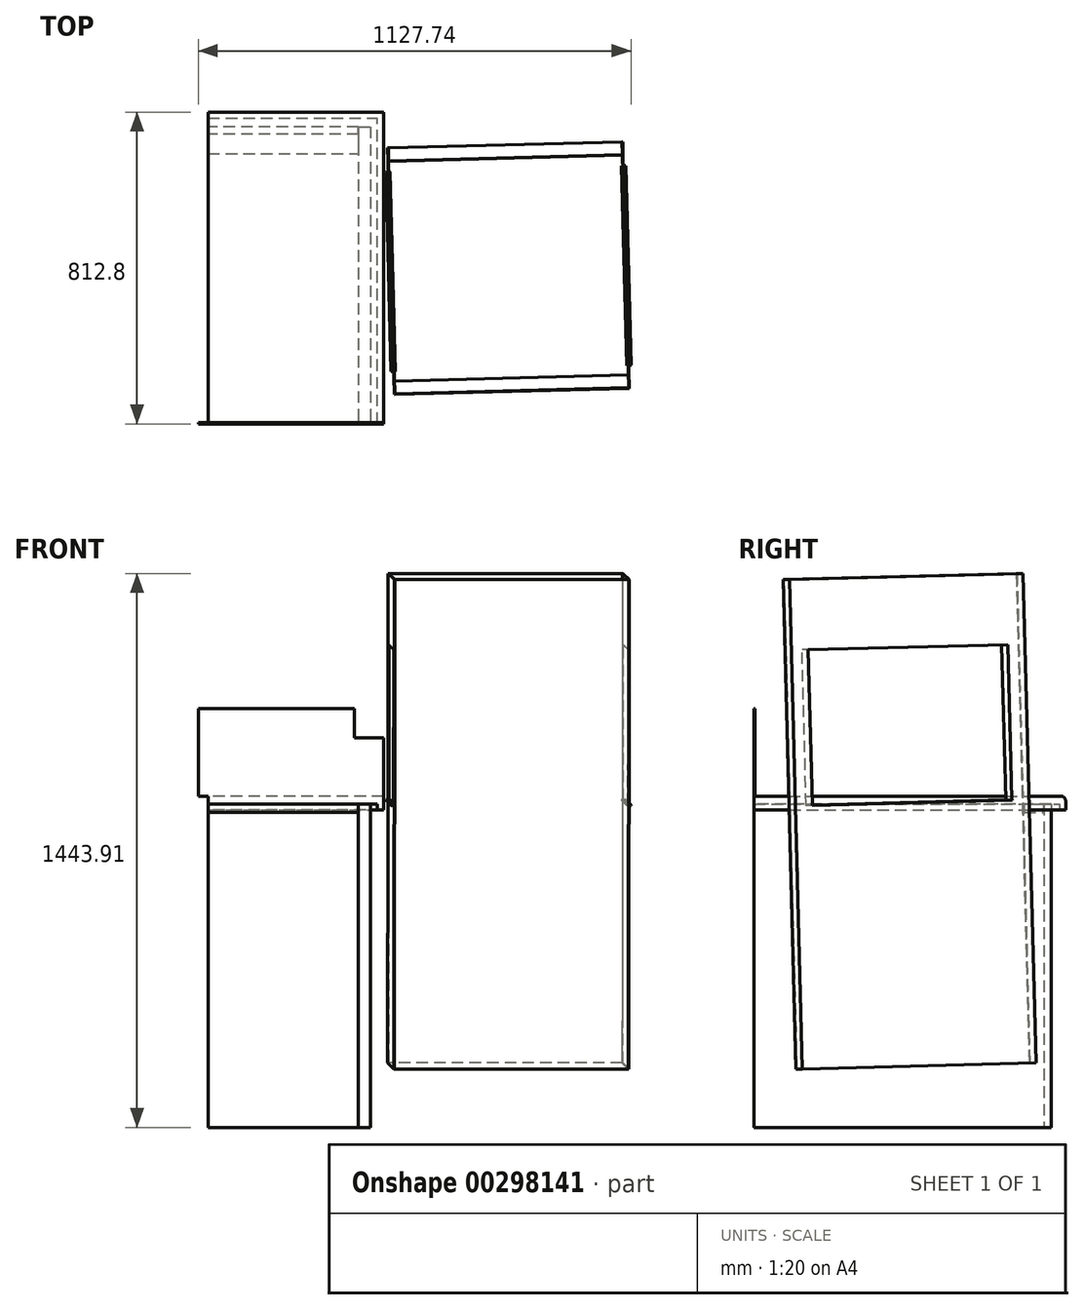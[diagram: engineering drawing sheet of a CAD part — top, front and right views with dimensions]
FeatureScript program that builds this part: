
annotation { "Feature Type Name" : "Feature", "Feature Type Description" : "" }
export const myFeature = defineFeature(function(context is Context, id is Id, definition is map)
    precondition{}
    {
        {
            var Q0;
            Q0=qCreatedBy(makeId("Top.planeOp"),FACE);
            cPlane(context, id + "F0", {"entities" : qUnion([Q0]), "cplaneType" : CPlaneType.OFFSET, "offset" : 863.6 * mm, "oppositeDirection" : true, "width" : 152.4 * mm, "height" : 152.4 * mm});
        }
        {
            var Q0;
            Q0=qCreatedBy(makeId("Right.planeOp"),FACE);
            var sketch = newSketch(context, id + "F1", { "sketchPlane" : qUnion([Q0])});
            skLineSegment(sketch, "E0.bottom", {"start": v(-406.4, 0) * mm, "end": v(393.7, 0) * mm});
            skLineSegment(sketch, "E0.top", {"start": v(-406.4, -36.51) * mm, "end": v(406.4, -36.51) * mm});
            skLineSegment(sketch, "E0.left", {"start": v(-406.4, 0) * mm, "end": v(-406.4, -36.51) * mm});
            skLineSegment(sketch, "E0.right", {"start": v(406.4, -12.7) * mm, "end": v(406.4, -36.51) * mm});
            skPoint(sketch, "E1.visualSharp", {"position": v(406.4, 0) * mm});
            skArc(sketch, "E1.filletArc", {"start": v(406.4, -12.7) * mm, "mid": v(402.68, -3.72) * mm, "end": v(393.7, 0) * mm});
            skSolve(sketch);
        }
        {
            var Q0;
            Q0 = qSketchRegion(id + "F1", true);
            extrude(context, id + "F2", {"entities" : qUnion([Q0]), "depth" : 457.2 * mm});
        }
        {
            var Q0;
            Q0=makeQuery(id+"F2.opExtrude","SWEPT_FACE",FACE,{"disambiguationData":[OSD([sQuery(id+"F1.wireOp",EDGE,"E0.top")])]});
            var sketch = newSketch(context, id + "F3", { "sketchPlane" : qUnion([Q0])});
            skLineSegment(sketch, "E2.bottom", {"start": v(0, 406.4) * mm, "end": v(441.33, 406.4) * mm});
            skLineSegment(sketch, "E2.top", {"start": v(0, -390.53) * mm, "end": v(441.33, -390.52) * mm});
            skLineSegment(sketch, "E2.left", {"start": v(0, 406.4) * mm, "end": v(0, -390.53) * mm});
            skLineSegment(sketch, "E2.right", {"start": v(441.33, 406.4) * mm, "end": v(441.33, -390.52) * mm});
            skSolve(sketch);
        }
        {
            var Q0;
            Q0 = qSketchRegion(id + "F3", true);
            extrude(context, id + "F4", {"entities" : qUnion([Q0]), "operationType" : NewBodyOperationType.REMOVE, "oppositeDirection" : true, "depth" : 15.88 * mm});
        }
        {
            var Q0;
            Q0=qCreatedBy(id+"F0.planeOp",FACE);
            var sketch = newSketch(context, id + "F5", { "sketchPlane" : qUnion([Q0])});
            skLineSegment(sketch, "E3", {"start": v(779.66, 121.89) * mm, "end": v(784.98, -81.25) * mm});
            skPoint(sketch, "E4", {"position": v(782.32, 20.32) * mm});
            skLineSegment(sketch, "E5", {"start": v(782.32, 223.52) * mm, "end": v(782.32, 20.32) * mm, "construction": true});
            skSolve(sketch);
        }
        {
            var Q0;
            Q0 = qSketchRegion(id + "F5", true);
            var Q1;
            Q1 = qConstructionFilter(qBodyType(qCreatedBy(id + "F5" ,EDGE), BodyType.WIRE), ConstructionObject.NO);
            extrude(context, id + "F6", {"entities" : qUnion([Q0]), "bodyType" : ToolBodyType.SURFACE, "surfaceEntities" : qUnion([Q1]), "depth" : 1524 * mm});
        }
        {
            var Q0;
            Q0=makeQuery(id+"F6.opExtrude","SWEPT_FACE",FACE,{"disambiguationData":[OSD([sQuery(id+"F5.wireOp",EDGE,"E3")])]});
            var sketch = newSketch(context, id + "F7", { "sketchPlane" : qUnion([Q0])});
            skLineSegment(sketch, "E6", {"start": v(0.17, -863.6) * mm, "end": v(40.07, 660.4) * mm});
            skSolve(sketch);
        }
        {
            var Q0;
            Q0 = qSketchRegion(id + "F7", true);
            var Q1;
            Q1=sQuery(id+"F7.wireOp",EDGE,"E6");
            extrude(context, id + "F8", {"entities" : qUnion([Q0]), "bodyType" : ToolBodyType.SURFACE, "surfaceEntities" : qUnion([Q1]), "endBound" : BoundingType.SYMMETRIC, "depth" : 203.2 * mm});
        }
        {
            var Q0;
            Q0=makeQuery(id+"F2.opExtrude","SWEPT_FACE",FACE,{"disambiguationData":[OSD([sQuery(id+"F1.wireOp",EDGE,"E0.left")])]});
            cPlane(context, id + "F9", {"entities" : qUnion([Q0]), "cplaneType" : CPlaneType.OFFSET, "offset" : 0 * mm, "width" : 152.4 * mm, "height" : 152.4 * mm});
        }
        {
            var Q0;
            Q0=qCreatedBy(id+"F9.planeOp",FACE);
            var sketch = newSketch(context, id + "F10", { "sketchPlane" : qUnion([Q0])});
            skLineSegment(sketch, "E7.bottom", {"start": v(457.2, 0) * mm, "end": v(274.53, 0) * mm});
            skLineSegment(sketch, "E7.top", {"start": v(457.2, 152.4) * mm, "end": v(381, 152.4) * mm});
            skLineSegment(sketch, "E7.left", {"start": v(457.2, 0) * mm, "end": v(457.2, 152.4) * mm});
            skLineSegment(sketch, "E8", {"start": v(381, 152.4) * mm, "end": v(381, 228.6) * mm});
            skLineSegment(sketch, "E9", {"start": v(381, 228.6) * mm, "end": v(-25.4, 228.6) * mm});
            skLineSegment(sketch, "E10", {"start": v(-25.4, 228.6) * mm, "end": v(-25.4, 0) * mm});
            skLineSegment(sketch, "E11", {"start": v(-25.4, 0) * mm, "end": v(274.53, 0) * mm});
            skSolve(sketch);
        }
        {
            var Q0;
            Q0=makeQuery(id+"F10.imprint","IMPRINT",FACE,{"disambiguationData":[TD([[makeQuery(id+"F10.imprint","IMPRINT",EDGE,{"derivedFrom":sQuery(id+"F10.wireOp",EDGE,"E7.bottom")}),-1.0]])]});
            extrude(context, id + "F11", {"entities" : qUnion([Q0]), "operationType" : NewBodyOperationType.ADD, "oppositeDirection" : true, "depth" : 3.17 * mm});
        }
        {
            var Q0;
            Q0=makeQuery(id+"F11.boolean.opBoolean","MERGE",FACE,{"derivedFrom":[makeQuery(id+"F2.opExtrude","CAP_FACE",FACE,{"disambiguationData":[OSD([sQuery(id+"F1.wireOp",EDGE,"E0.bottom"),sQuery(id+"F1.wireOp",EDGE,"E0.top"),sQuery(id+"F1.wireOp",EDGE,"E0.left"),sQuery(id+"F1.wireOp",EDGE,"E0.right"),sQuery(id+"F1.wireOp",EDGE,"E1.filletArc")])],"isStart":false}),makeQuery(id+"F11.opExtrude","SWEPT_FACE",FACE,{"disambiguationData":[OSD([sQuery(id+"F10.wireOp",EDGE,"E7.left")])]})]});
            cPlane(context, id + "F12", {"entities" : qUnion([Q0]), "cplaneType" : CPlaneType.OFFSET, "offset" : 33.34 * mm, "oppositeDirection" : true, "width" : 152.4 * mm, "height" : 152.4 * mm});
        }
        {
            var Q0;
            Q0=qCreatedBy(id+"F12.planeOp",FACE);
            var sketch = newSketch(context, id + "F13", { "sketchPlane" : qUnion([Q0])});
            skLineSegment(sketch, "E12.bottom", {"start": v(368.3, -20.64) * mm, "end": v(-406.4, -20.64) * mm});
            skLineSegment(sketch, "E12.top", {"start": v(368.3, -863.6) * mm, "end": v(-406.4, -863.6) * mm});
            skLineSegment(sketch, "E12.left", {"start": v(368.3, -20.64) * mm, "end": v(368.3, -863.6) * mm});
            skLineSegment(sketch, "E12.right", {"start": v(-406.4, -20.64) * mm, "end": v(-406.4, -863.6) * mm});
            skSolve(sketch);
        }
        {
            var Q0;
            Q0 = qSketchRegion(id + "F13", true);
            extrude(context, id + "F14", {"entities" : qUnion([Q0]), "oppositeDirection" : true, "depth" : 31.75 * mm});
        }
        {
            var Q0;
            Q0=makeQuery(id+"F6.opExtrude","SWEPT_FACE",FACE,{"disambiguationData":[OSD([sQuery(id+"F5.wireOp",EDGE,"E3")])]});
            cPlane(context, id + "F15", {"entities" : qUnion([Q0]), "cplaneType" : CPlaneType.OFFSET, "offset" : 304.8 * mm, "width" : 152.4 * mm, "height" : 152.4 * mm});
        }
        {
            var Q0;
            Q0=qCreatedBy(id+"F15.planeOp",FACE);
            var sketch = newSketch(context, id + "F16", { "sketchPlane" : qUnion([Q0])});
            skLineSegment(sketch, "E13.bottom", {"start": v(-300.34, -695.6) * mm, "end": v(309.05, -711.56) * mm});
            skLineSegment(sketch, "E13.top", {"start": v(342.46, 564.35) * mm, "end": v(-266.93, 580.31) * mm});
            skLineSegment(sketch, "E13.left", {"start": v(-300.34, -695.6) * mm, "end": v(-266.93, 580.31) * mm});
            skLineSegment(sketch, "E13.right", {"start": v(309.05, -711.56) * mm, "end": v(342.46, 564.35) * mm});
            skLineSegment(sketch, "E14.bottom", {"start": v(-237.95, -11.2) * mm, "end": v(282.57, -24.83) * mm});
            skLineSegment(sketch, "E14.top", {"start": v(-227.31, 395.06) * mm, "end": v(293.2, 381.43) * mm});
            skLineSegment(sketch, "E14.left", {"start": v(-237.95, -11.2) * mm, "end": v(-227.31, 395.06) * mm});
            skLineSegment(sketch, "E14.right", {"start": v(282.57, -24.83) * mm, "end": v(293.2, 381.43) * mm});
            skPoint(sketch, "E15", {"position": v(22.3, -18.02) * mm});
            skPoint(sketch, "E16", {"position": v(4.36, -703.58) * mm});
            skPoint(sketch, "E17", {"position": v(327, -26) * mm});
            skSolve(sketch);
        }
        {
            var Q0;
            Q0 = qSketchRegion(id + "F16", true);
            extrude(context, id + "F17", {"entities" : qUnion([Q0]), "depth" : 1.59 * mm});
        }
        {
            var Q0;
            Q0=makeQuery(id+"F17.opExtrude","SWEPT_BODY",BODY,{"disambiguationData":[OSD([sQuery(id+"F16.wireOp",EDGE,"E13.bottom"),sQuery(id+"F16.wireOp",EDGE,"E13.top"),sQuery(id+"F16.wireOp",EDGE,"E13.left"),sQuery(id+"F16.wireOp",EDGE,"E13.right"),sQuery(id+"F16.wireOp",EDGE,"E14.top"),sQuery(id+"F16.wireOp",EDGE,"E14.left"),sQuery(id+"F16.wireOp",EDGE,"E14.right")])]});
            var Q1;
            Q1=makeQuery(id+"F6.opExtrude","SWEPT_FACE",FACE,{"disambiguationData":[OSD([sQuery(id+"F5.wireOp",EDGE,"E3")])]});
            mirror(context, id + "F18", {"entities" : qUnion([Q0]), "mirrorPlane" : qUnion([Q1])});
        }
        {
            var Q0;
            Q0=makeQuery(id+"F8.opExtrude","SWEPT_FACE",FACE,{"disambiguationData":[OSD([sQuery(id+"F7.wireOp",EDGE,"E6")])]});
            var Q1;
            Q1=makeQuery(id+"F17.opExtrude","CAP_VERTEX",VERTEX,{"disambiguationData":[OSD([sQuery(id+"F16.wireOp",EDGE,"E13.top"),sQuery(id+"F16.wireOp",EDGE,"E13.left")])],"isStart":false});
            cPlane(context, id + "F19", {"entities" : qUnion([Q0, Q1]), "cplaneType" : CPlaneType.PLANE_POINT, "offset" : 299.72 * mm, "oppositeDirection" : true, "width" : 152.4 * mm, "height" : 152.4 * mm});
        }
        {
            var Q0;
            Q0=qCreatedBy(id+"F19.planeOp",FACE);
            var sketch = newSketch(context, id + "F20", { "sketchPlane" : qUnion([Q0])});
            skLineSegment(sketch, "E18.bottom", {"start": v(1087.78, 572.38) * mm, "end": v(478.18, 572.8) * mm});
            skLineSegment(sketch, "E18.top", {"start": v(1086.9, -703.97) * mm, "end": v(477.3, -703.55) * mm});
            skLineSegment(sketch, "E18.left", {"start": v(1087.78, 572.38) * mm, "end": v(1086.9, -703.97) * mm});
            skLineSegment(sketch, "E18.right", {"start": v(478.18, 572.8) * mm, "end": v(477.3, -703.55) * mm});
            skSolve(sketch);
        }
        {
            var Q0;
            Q0 = qSketchRegion(id + "F20", true);
            extrude(context, id + "F21", {"entities" : qUnion([Q0]), "depth" : 1.59 * mm});
        }
        {
            var Q0;
            Q0=makeQuery(id+"F21.opExtrude","SWEPT_BODY",BODY,{"disambiguationData":[OSD([sQuery(id+"F20.wireOp",EDGE,"E18.bottom"),sQuery(id+"F20.wireOp",EDGE,"E18.top"),sQuery(id+"F20.wireOp",EDGE,"E18.left"),sQuery(id+"F20.wireOp",EDGE,"E18.right")])]});
            var Q1;
            Q1=makeQuery(id+"F8.opExtrude","SWEPT_FACE",FACE,{"disambiguationData":[OSD([sQuery(id+"F7.wireOp",EDGE,"E6")])]});
            mirror(context, id + "F22", {"entities" : qUnion([Q0]), "mirrorPlane" : qUnion([Q1])});
        }
        {
            var Q0;
            Q0=makeQuery(id+"F14.opExtrude","SWEPT_FACE",FACE,{"disambiguationData":[OSD([sQuery(id+"F13.wireOp",EDGE,"E12.left")])]});
            var sketch = newSketch(context, id + "F23", { "sketchPlane" : qUnion([Q0])});
            skLineSegment(sketch, "E19.bottom", {"start": v(-392.11, -20.64) * mm, "end": v(0, -20.64) * mm});
            skLineSegment(sketch, "E19.top", {"start": v(-392.11, -863.6) * mm, "end": v(0, -863.6) * mm});
            skLineSegment(sketch, "E19.left", {"start": v(-392.11, -20.64) * mm, "end": v(-392.11, -863.6) * mm});
            skLineSegment(sketch, "E19.right", {"start": v(0, -20.64) * mm, "end": v(0, -863.6) * mm});
            skSolve(sketch);
        }
        {
            var Q0;
            Q0 = qSketchRegion(id + "F23", true);
            extrude(context, id + "F24", {"entities" : qUnion([Q0]), "oppositeDirection" : true, "depth" : 19.05 * mm});
        }
        {
            var Q0;
            Q0=makeQuery(id+"F14.opExtrude","CAP_FACE",FACE,{"disambiguationData":[OSD([sQuery(id+"F13.wireOp",EDGE,"E12.bottom"),sQuery(id+"F13.wireOp",EDGE,"E12.top"),sQuery(id+"F13.wireOp",EDGE,"E12.left"),sQuery(id+"F13.wireOp",EDGE,"E12.right")])],"isStart":false});
            var sketch = newSketch(context, id + "F25", { "sketchPlane" : qUnion([Q0])});
            skLineSegment(sketch, "E20.bottom", {"start": v(-349.25, -20.64) * mm, "end": v(-298.45, -20.64) * mm});
            skLineSegment(sketch, "E20.top", {"start": v(-349.25, -42.86) * mm, "end": v(-298.45, -42.86) * mm});
            skLineSegment(sketch, "E20.left", {"start": v(-349.25, -20.64) * mm, "end": v(-349.25, -42.86) * mm});
            skLineSegment(sketch, "E20.right", {"start": v(-298.45, -20.64) * mm, "end": v(-298.45, -42.86) * mm});
            skSolve(sketch);
        }
        {
            var Q0;
            Q0 = qSketchRegion(id + "F25", true);
            var Q1;
            Q1=makeQuery(id+"F24.boolean.opBoolean","MERGE",FACE,{"derivedFrom":[makeQuery(id+"F2.opExtrude","CAP_FACE",FACE,{"disambiguationData":[OSD([sQuery(id+"F1.wireOp",EDGE,"E0.bottom"),sQuery(id+"F1.wireOp",EDGE,"E0.top"),sQuery(id+"F1.wireOp",EDGE,"E0.left"),sQuery(id+"F1.wireOp",EDGE,"E0.right"),sQuery(id+"F1.wireOp",EDGE,"E1.filletArc")])],"isStart":true}),makeQuery(id+"F24.opExtrude","SWEPT_FACE",FACE,{"disambiguationData":[OSD([sQuery(id+"F23.wireOp",EDGE,"E19.right")])]})]});
            extrude(context, id + "F26", {"entities" : qUnion([Q0]), "endBound" : BoundingType.UP_TO_SURFACE, "endBoundEntityFace" : qUnion([Q1]), "depth" : 25.4 * mm});
        }
        {
            var Q0;
            Q0=makeQuery(id+"F18.opPattern","COPY",FACE,{"derivedFrom":makeQuery(id+"F17.opExtrude","SWEPT_FACE",FACE,{"disambiguationData":[OSD([sQuery(id+"F16.wireOp",EDGE,"E14.bottom")])]}),"instanceName":"1"});
            var sketch = newSketch(context, id + "F27", { "sketchPlane" : qUnion([Q0])});
            skLineSegment(sketch, "E21.bottom", {"start": v(1102.35, -254.36) * mm, "end": v(1091.25, -254.65) * mm});
            skLineSegment(sketch, "E21.top", {"start": v(1088.73, 266.16) * mm, "end": v(1077.62, 265.87) * mm});
            skLineSegment(sketch, "E21.left", {"start": v(1102.35, -254.36) * mm, "end": v(1088.73, 266.16) * mm});
            skLineSegment(sketch, "E21.right", {"start": v(1091.25, -254.65) * mm, "end": v(1077.62, 265.87) * mm});
            skSolve(sketch);
        }
        {
            var Q0;
            Q0 = qSketchRegion(id + "F27", true);
            extrude(context, id + "F28", {"entities" : qUnion([Q0]), "depth" : 1.52 * mm});
        }
        {
            var Q0;
            Q0=makeQuery(id+"F28.opExtrude","SWEPT_BODY",BODY,{"disambiguationData":[OSD([sQuery(id+"F27.wireOp",EDGE,"E21.bottom"),sQuery(id+"F27.wireOp",EDGE,"E21.top"),sQuery(id+"F27.wireOp",EDGE,"E21.left"),sQuery(id+"F27.wireOp",EDGE,"E21.right")])]});
            var Q1;
            Q1=makeQuery(id+"F6.opExtrude","SWEPT_FACE",FACE,{"disambiguationData":[OSD([sQuery(id+"F5.wireOp",EDGE,"E3")])]});
            mirror(context, id + "F29", {"operationType" : NewBodyOperationType.ADD, "entities" : qUnion([Q0]), "mirrorPlane" : qUnion([Q1])});
        }
    });
